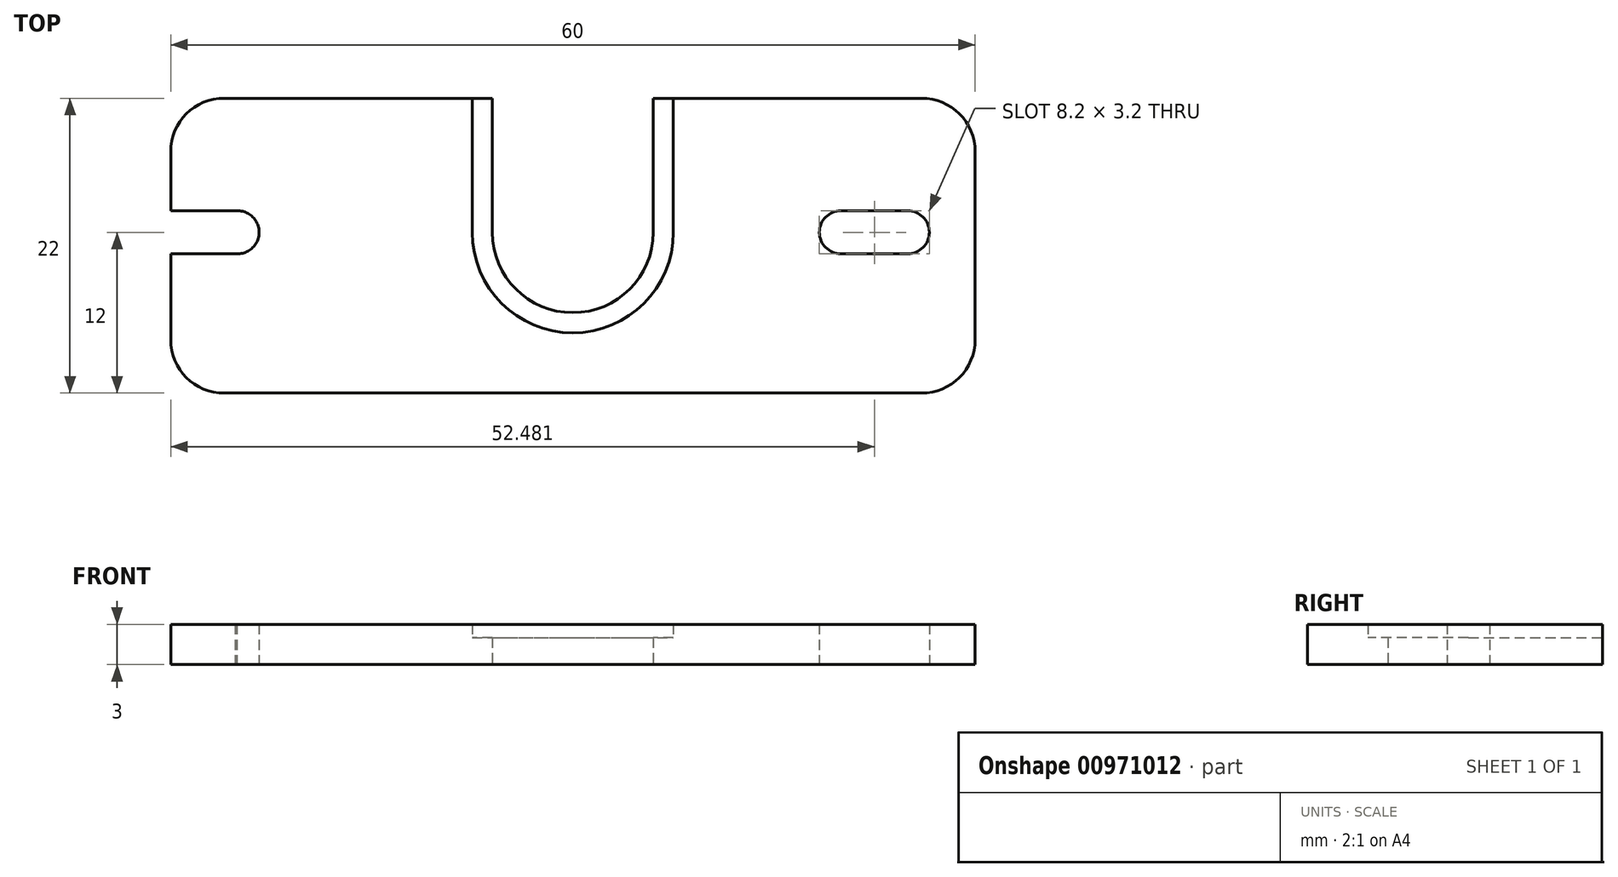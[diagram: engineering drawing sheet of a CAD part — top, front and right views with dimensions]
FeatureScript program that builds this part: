
annotation { "Feature Type Name" : "Feature", "Feature Type Description" : "" }
export const myFeature = defineFeature(function(context is Context, id is Id, definition is map)
    precondition{}
    {
        {
            var Q0;
            Q0=qCreatedBy(makeId("Top.planeOp"),FACE);
            var sketch = newSketch(context, id + "F0", { "sketchPlane" : qUnion([Q0])});
            skLineSegment(sketch, "E0.bottom", {"start": v(26, -11) * mm, "end": v(-26, -11) * mm});
            skLineSegment(sketch, "E0.top", {"start": v(26, 11) * mm, "end": v(6, 11) * mm});
            skLineSegment(sketch, "E0.left", {"start": v(30, -7) * mm, "end": v(30, 7) * mm});
            skLineSegment(sketch, "E0.right", {"start": v(-30, -7) * mm, "end": v(-30, -0.59) * mm});
            skPoint(sketch, "E0.middle", {"position": v(0, 1) * mm});
            skPoint(sketch, "E1.visualSharp", {"position": v(-30, 11) * mm});
            skArc(sketch, "E1.filletArc", {"start": v(-26, 11) * mm, "mid": v(-28.83, 9.83) * mm, "end": v(-30, 7) * mm});
            skPoint(sketch, "E2.visualSharp", {"position": v(30, 11) * mm});
            skArc(sketch, "E2.filletArc", {"start": v(30, 7) * mm, "mid": v(28.83, 9.83) * mm, "end": v(26, 11) * mm});
            skPoint(sketch, "E3.visualSharp", {"position": v(30, -11) * mm});
            skArc(sketch, "E3.filletArc", {"start": v(26, -11) * mm, "mid": v(28.83, -9.83) * mm, "end": v(30, -7) * mm});
            skPoint(sketch, "E4.visualSharp", {"position": v(-30, -11) * mm});
            skArc(sketch, "E4.filletArc", {"start": v(-30, -7) * mm, "mid": v(-28.83, -9.83) * mm, "end": v(-26, -11) * mm});
            skLineSegment(sketch, "E5", {"start": v(-25, 1) * mm, "end": v(24.98, 1) * mm, "construction": true});
            skArc(sketch, "E6", {"start": v(-6, 1) * mm, "mid": v(0, -5) * mm, "end": v(6, 1) * mm});
            skArc(sketch, "E7", {"start": v(24.98, -0.6) * mm, "mid": v(26.58, 1) * mm, "end": v(24.98, 2.6) * mm});
            skArc(sketch, "E8", {"start": v(-25.18, -0.59) * mm, "mid": v(-23.4, 0.95) * mm, "end": v(-25.07, 2.6) * mm});
            skLineSegment(sketch, "E9", {"start": v(-6, 1) * mm, "end": v(-6, 11) * mm});
            skLineSegment(sketch, "E10", {"start": v(6, 11) * mm, "end": v(6, 1) * mm});
            skLineSegment(sketch, "E11", {"start": v(-24.93, 2.6) * mm, "end": v(-30, 2.6) * mm});
            skLineSegment(sketch, "E12", {"start": v(-25.18, -0.59) * mm, "end": v(-30, -0.59) * mm});
            skArc(sketch, "E13", {"start": v(19.98, 2.6) * mm, "mid": v(18.38, 1) * mm, "end": v(19.98, -0.6) * mm});
            skLineSegment(sketch, "E14", {"start": v(19.98, 2.6) * mm, "end": v(24.98, 2.6) * mm});
            skLineSegment(sketch, "E15", {"start": v(24.98, -0.6) * mm, "end": v(19.98, -0.6) * mm});
            skLineSegment(sketch, "E16.trimOffspring", {"start": v(-6, 11) * mm, "end": v(-26, 11) * mm});
            skLineSegment(sketch, "E17.trimOffspring", {"start": v(-30, 2.6) * mm, "end": v(-30, 7) * mm});
            skLineSegment(sketch, "E18.0", {"start": v(-7.5, 1) * mm, "end": v(-7.5, 11) * mm});
            skArc(sketch, "E18.1", {"start": v(-7.5, 1) * mm, "mid": v(0, -6.5) * mm, "end": v(7.5, 1) * mm});
            skLineSegment(sketch, "E18.2", {"start": v(7.5, 11) * mm, "end": v(7.5, 1) * mm});
            skSolve(sketch);
        }
        {
            var Q0;
            Q0=makeQuery(id+"F0.imprint","IMPRINT",FACE,{"disambiguationData":[TD([[makeQuery(id+"F0.imprint","IMPRINT",EDGE,{"derivedFrom":sQuery(id+"F0.wireOp",EDGE,"E0.bottom")}),-1.0]])]});
            extrude(context, id + "F1", {"entities" : qUnion([Q0]), "depth" : 3 * mm, "offsetDistance" : 25 * mm});
        }
        {
            var Q0;
            Q0=makeQuery(id+"F0.imprint","IMPRINT",FACE,{"disambiguationData":[TD([[makeQuery(id+"F0.imprint","IMPRINT",EDGE,{"derivedFrom":sQuery(id+"F0.wireOp",EDGE,"E6")}),-1.0]])]});
            extrude(context, id + "F2", {"entities" : qUnion([Q0]), "operationType" : NewBodyOperationType.ADD, "depth" : 2 * mm, "offsetDistance" : 25 * mm});
        }
    });
